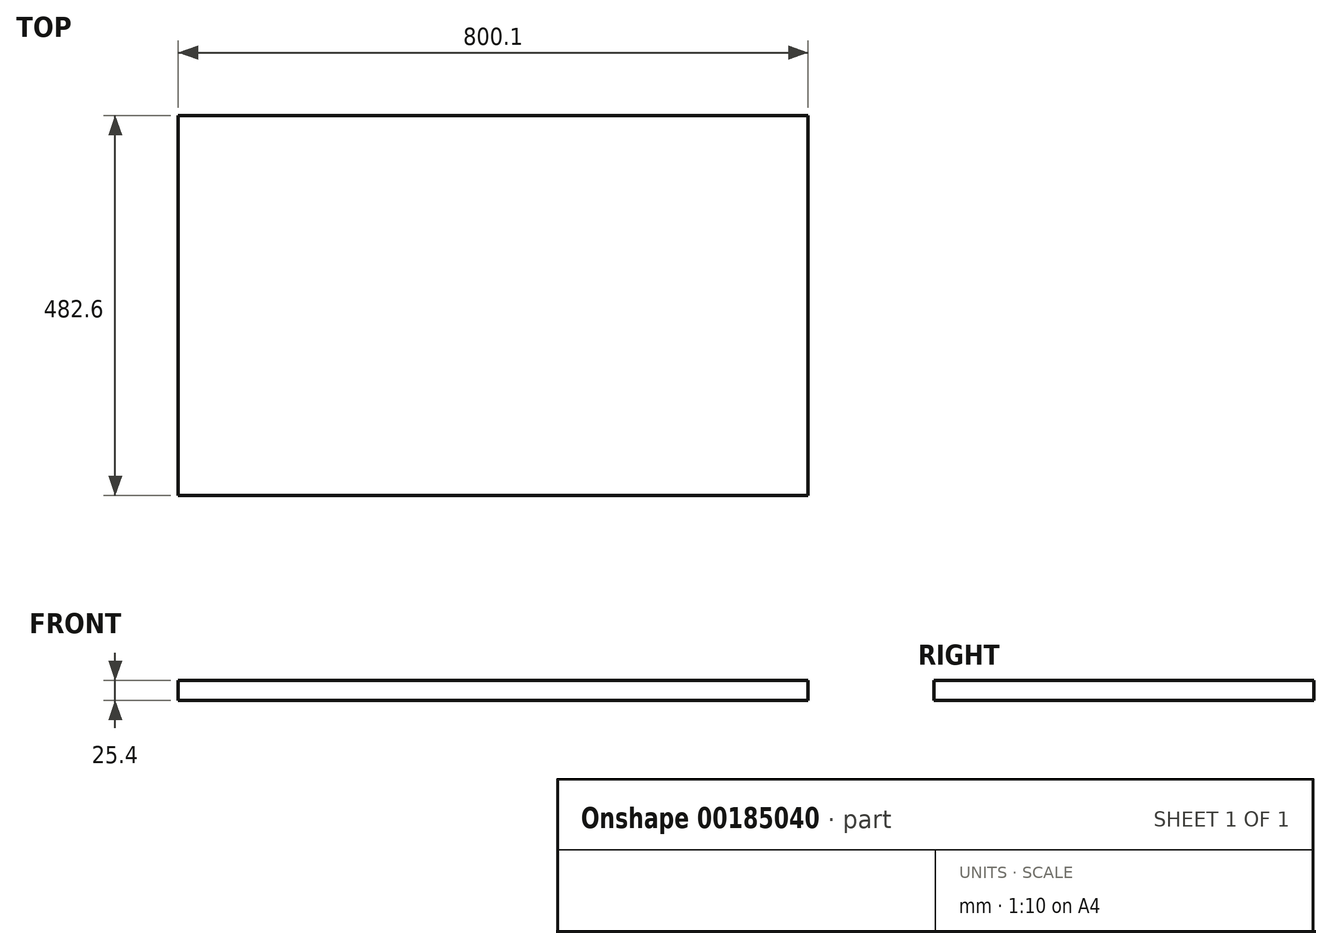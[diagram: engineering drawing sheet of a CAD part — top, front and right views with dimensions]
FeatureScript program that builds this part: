
annotation { "Feature Type Name" : "Feature", "Feature Type Description" : "" }
export const myFeature = defineFeature(function(context is Context, id is Id, definition is map)
    precondition{}
    {
        {
            var Q0;
            Q0=qCreatedBy(makeId("Top.planeOp"),FACE);
            var sketch = newSketch(context, id + "F0", { "sketchPlane" : qUnion([Q0])});
            skLineSegment(sketch, "E0.bottom", {"start": v(400.05, 241.3) * mm, "end": v(-400.05, 241.3) * mm});
            skLineSegment(sketch, "E0.top", {"start": v(400.05, -241.3) * mm, "end": v(-400.05, -241.3) * mm});
            skLineSegment(sketch, "E0.left", {"start": v(400.05, 241.3) * mm, "end": v(400.05, -241.3) * mm});
            skLineSegment(sketch, "E0.right", {"start": v(-400.05, 241.3) * mm, "end": v(-400.05, -241.3) * mm});
            skPoint(sketch, "E0.middle", {"position": v(0, 0) * mm});
            skSolve(sketch);
        }
        {
            var Q0;
            Q0 = qSketchRegion(id + "F0", true);
            extrude(context, id + "F1", {"entities" : qUnion([Q0]), "depth" : 25.4 * mm});
        }
    });
